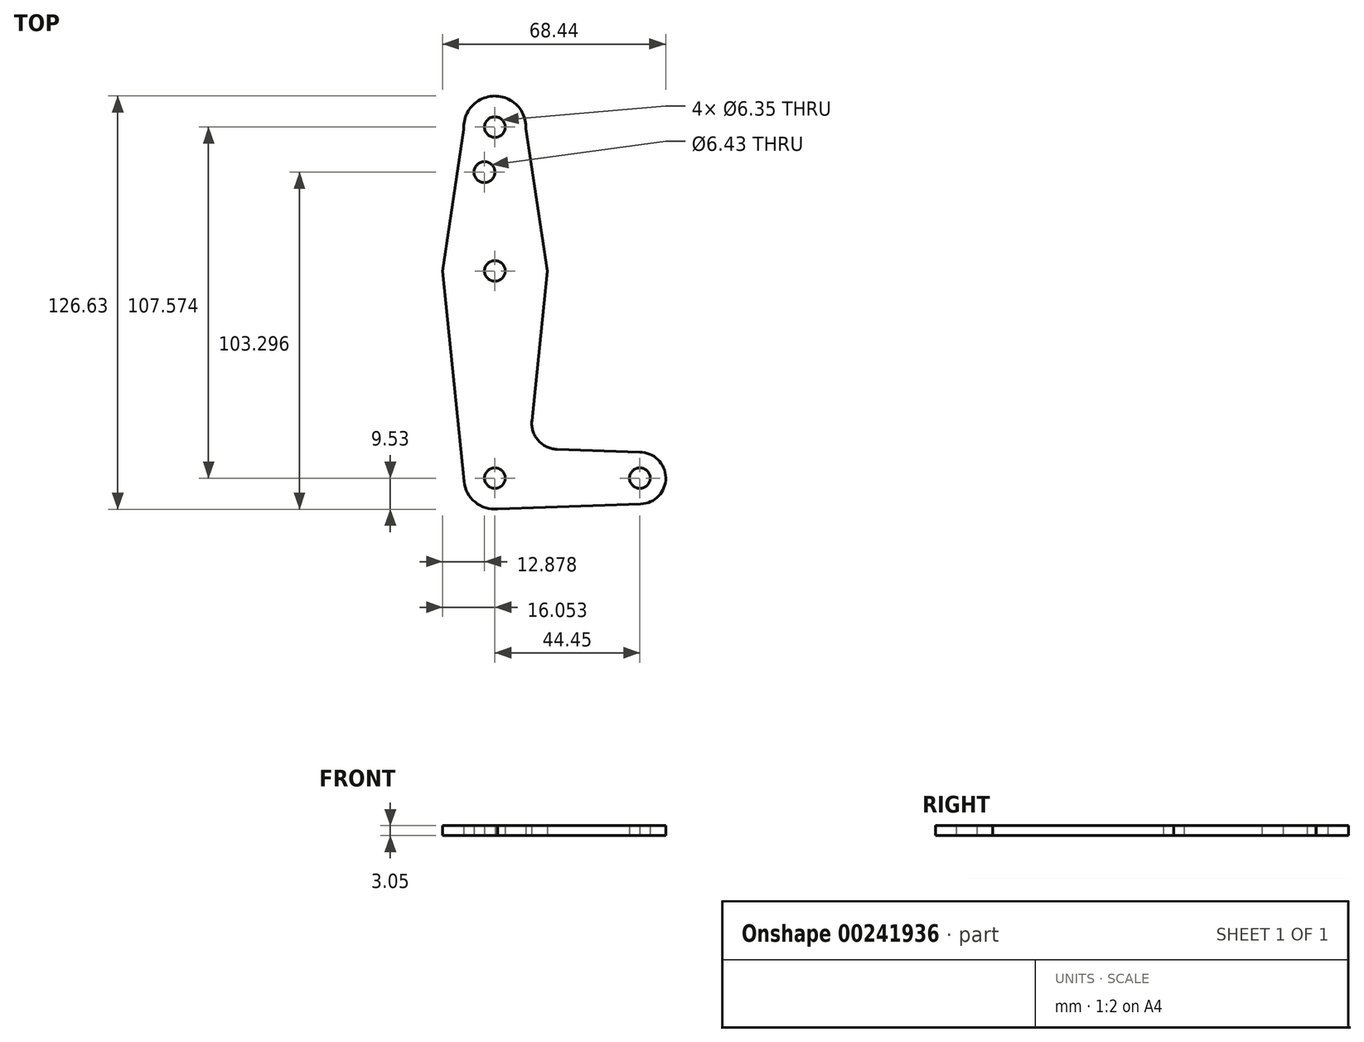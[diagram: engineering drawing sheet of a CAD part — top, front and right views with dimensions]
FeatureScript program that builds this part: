
annotation { "Feature Type Name" : "Feature", "Feature Type Description" : "" }
export const myFeature = defineFeature(function(context is Context, id is Id, definition is map)
    precondition{}
    {
        {
            var Q0;
            Q0=qCreatedBy(makeId("Top.planeOp"),FACE);
            var sketch = newSketch(context, id + "F0", { "sketchPlane" : qUnion([Q0])});
            skCircle(sketch, "E0", {"center": v(11.32, 44.07) * mm, "radius": 9.53 * mm});
            skCircle(sketch, "E1", {"center": v(11.32, 0) * mm, "radius": 15.88 * mm});
            skCircle(sketch, "E2", {"center": v(11.32, -63.5) * mm, "radius": 9.53 * mm});
            skLineSegment(sketch, "E3", {"start": v(2.48, 47.61) * mm, "end": v(-4.73, 0) * mm});
            skLineSegment(sketch, "E4", {"start": v(-4.73, 0) * mm, "end": v(1.85, -64.47) * mm});
            skCircle(sketch, "E5", {"center": v(55.77, -63.5) * mm, "radius": 7.94 * mm});
            skLineSegment(sketch, "E6", {"start": v(12.2, -72.98) * mm, "end": v(56.05, -71.43) * mm});
            skLineSegment(sketch, "E7", {"start": v(20.29, 47.3) * mm, "end": v(27.38, 0) * mm});
            skLineSegment(sketch, "E8", {"start": v(22.67, -45.9) * mm, "end": v(27.38, 0) * mm});
            skLineSegment(sketch, "E9", {"start": v(55.71, -55.56) * mm, "end": v(30.3, -54.65) * mm});
            skCircle(sketch, "E10", {"center": v(11.32, 44.07) * mm, "radius": 3.18 * mm});
            skCircle(sketch, "E11", {"center": v(11.32, 0) * mm, "radius": 3.18 * mm});
            skCircle(sketch, "E12", {"center": v(11.32, -63.5) * mm, "radius": 3.18 * mm});
            skCircle(sketch, "E13", {"center": v(55.77, -63.5) * mm, "radius": 3.18 * mm});
            skCircle(sketch, "E14", {"center": v(8.15, 30.27) * mm, "radius": 3.22 * mm});
            skArc(sketch, "E15.filletArc", {"start": v(22.67, -45.9) * mm, "mid": v(24.58, -51.93) * mm, "end": v(30.3, -54.65) * mm});
            skSolve(sketch);
        }
        {
            var Q0;
            Q0 = qSketchRegion(id + "F0", true);
            extrude(context, id + "F1", {"entities" : qUnion([Q0]), "depth" : 3.05 * mm});
        }
    });
